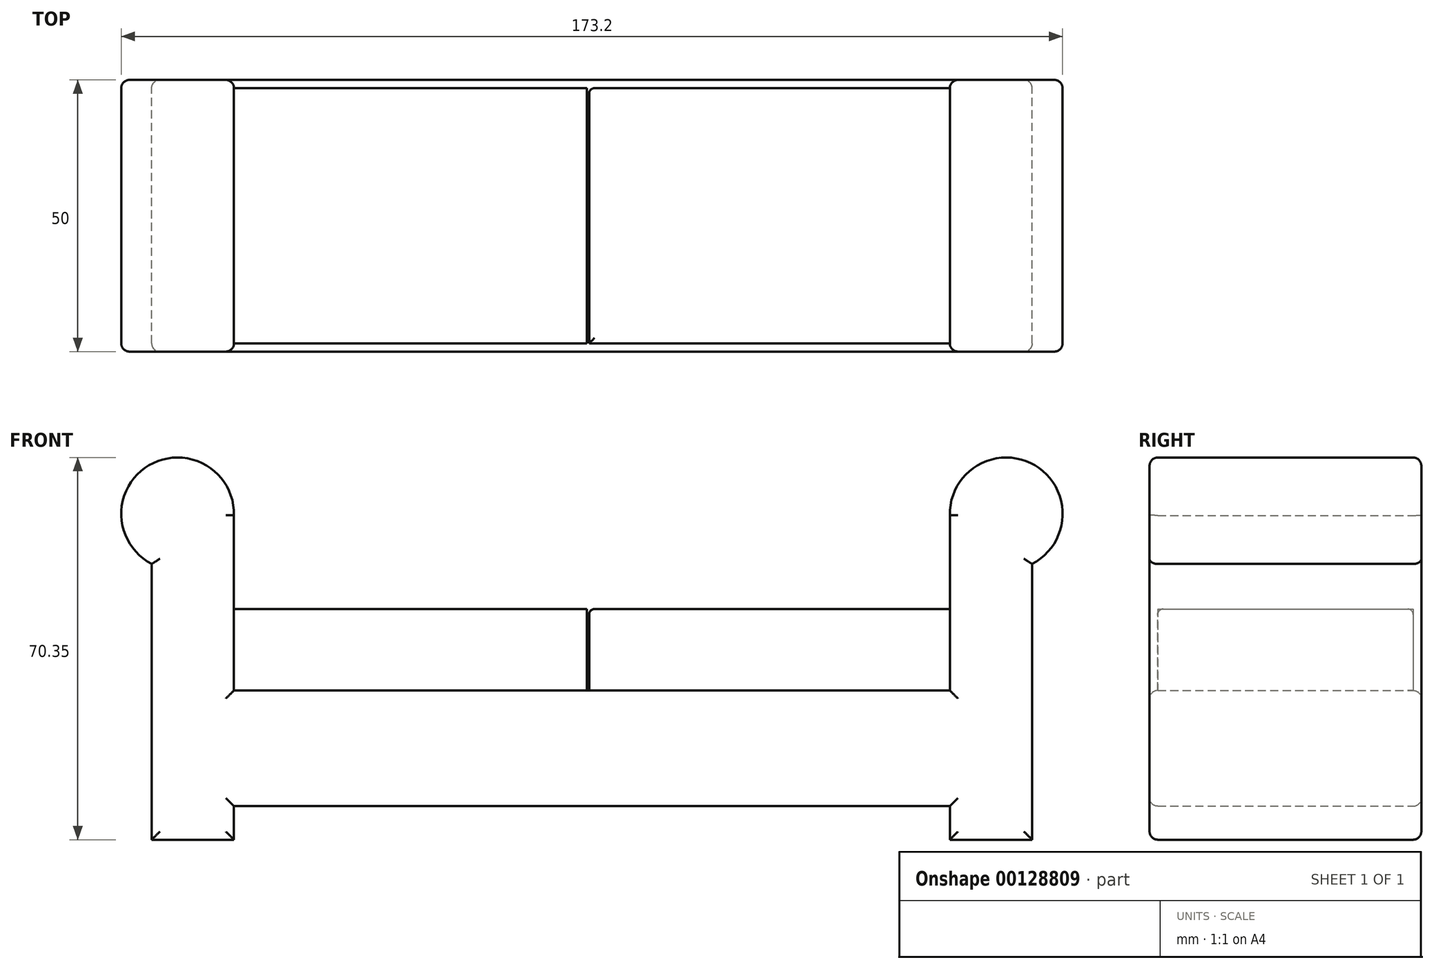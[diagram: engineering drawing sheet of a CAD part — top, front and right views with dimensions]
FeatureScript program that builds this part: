
annotation { "Feature Type Name" : "Feature", "Feature Type Description" : "" }
export const myFeature = defineFeature(function(context is Context, id is Id, definition is map)
    precondition{}
    {
        {
            var Q0;
            Q0=qCreatedBy(makeId("Front.planeOp"),FACE);
            var sketch = newSketch(context, id + "F0", { "sketchPlane" : qUnion([Q0])});
            skLineSegment(sketch, "E0.top", {"start": v(-65.16, -24.52) * mm, "end": v(66.56, -24.52) * mm});
            skLineSegment(sketch, "E0.left", {"start": v(-65.16, 24.24) * mm, "end": v(-65.16, -24.52) * mm});
            skLineSegment(sketch, "E0.right", {"start": v(66.56, -3.22) * mm, "end": v(66.56, -24.52) * mm});
            skPoint(sketch, "E0.middle", {"position": v(0.7, -0.14) * mm});
            skLineSegment(sketch, "E1.bottom", {"start": v(-65.16, -30.69) * mm, "end": v(-80.3, -30.69) * mm});
            skLineSegment(sketch, "E1.left", {"start": v(-65.16, -30.69) * mm, "end": v(-65.16, 29) * mm});
            skLineSegment(sketch, "E1.right", {"start": v(-80.3, -30.69) * mm, "end": v(-80.3, 20.07) * mm});
            skArc(sketch, "E2", {"start": v(-65.16, 29) * mm, "mid": v(-80.8, 38.21) * mm, "end": v(-80.3, 20.07) * mm});
            skPoint(sketch, "E2.second.point", {"position": v(-85.9, 29) * mm});
            skPoint(sketch, "E2.third.point", {"position": v(-75.53, 39.66) * mm});
            skPoint(sketch, "E3.orphan", {"position": v(-80.3, 29) * mm});
            skLineSegment(sketch, "E4", {"start": v(-65.16, -3.22) * mm, "end": v(66.56, -3.22) * mm});
            skPoint(sketch, "E0.bottom.end.orphan", {"position": v(66.56, 24.24) * mm});
            skLineSegment(sketch, "E5", {"start": v(0.7, -3.22) * mm, "end": v(0.7, -24.52) * mm, "construction": true});
            skLineSegment(sketch, "E6.MirrorCS", {"start": v(66.56, 24.24) * mm, "end": v(66.56, -24.52) * mm});
            skPoint(sketch, "E7.MirrorP", {"position": v(76.93, 39.66) * mm});
            skLineSegment(sketch, "E8.MirrorCS", {"start": v(81.7, -30.69) * mm, "end": v(81.7, 20.07) * mm});
            skLineSegment(sketch, "E9.MirrorCS", {"start": v(66.56, -30.69) * mm, "end": v(66.56, 29) * mm});
            skArc(sketch, "E10.MirrorCS", {"start": v(66.56, 29) * mm, "mid": v(82.2, 38.21) * mm, "end": v(81.7, 20.07) * mm});
            skPoint(sketch, "E11.MirrorP", {"position": v(81.7, 29) * mm});
            skPoint(sketch, "E12.MirrorP", {"position": v(87.3, 29) * mm});
            skLineSegment(sketch, "E13.MirrorCS", {"start": v(66.56, -30.69) * mm, "end": v(81.7, -30.69) * mm});
            skSolve(sketch);
        }
        {
            var Q0;
            Q0 = qSketchRegion(id + "F0", true);
            extrude(context, id + "F1", {"entities" : qUnion([Q0]), "endBound" : BoundingType.SYMMETRIC, "depth" : 50 * mm, "offsetDistance" : 25 * mm});
        }
        {
            var Q0;
            Q0=makeQuery(id+"F1.opExtrude","CAP_FACE",FACE,{"disambiguationData":[OSD([sQuery(id+"F0.wireOp",EDGE,"E0.top"),sQuery(id+"F0.wireOp",EDGE,"E0.right"),sQuery(id+"F0.wireOp",EDGE,"E1.bottom"),sQuery(id+"F0.wireOp",EDGE,"E1.left"),sQuery(id+"F0.wireOp",EDGE,"E1.right"),sQuery(id+"F0.wireOp",EDGE,"E2"),sQuery(id+"F0.wireOp",EDGE,"E4")])],"isStart":false});
            var Q1;
            Q1=makeQuery(id+"F1.opExtrude","CAP_FACE",FACE,{"disambiguationData":[OSD([sQuery(id+"F0.wireOp",EDGE,"E0.top"),sQuery(id+"F0.wireOp",EDGE,"E1.bottom"),sQuery(id+"F0.wireOp",EDGE,"E1.left"),sQuery(id+"F0.wireOp",EDGE,"E1.right"),sQuery(id+"F0.wireOp",EDGE,"E2"),sQuery(id+"F0.wireOp",EDGE,"E4"),sQuery(id+"F0.wireOp",EDGE,"E8.MirrorCS"),sQuery(id+"F0.wireOp",EDGE,"E9.MirrorCS"),sQuery(id+"F0.wireOp",EDGE,"E10.MirrorCS"),sQuery(id+"F0.wireOp",EDGE,"E13.MirrorCS")])],"isStart":true});
            fillet(context, id + "F2", {"entities" : qUnion([Q0, Q1]), "radius" : 1.5 * mm, "tangentPropagation" : true, "allowEdgeOverflow" : false});
        }
        {
            var Q0;
            Q0=makeQuery(id+"F1.opExtrude","SWEPT_FACE",FACE,{"disambiguationData":[OSD([sQuery(id+"F0.wireOp",EDGE,"E4")])]});
            var sketch = newSketch(context, id + "F3", { "sketchPlane" : qUnion([Q0])});
            skLineSegment(sketch, "E14.bottom", {"start": v(-65.16, -23.5) * mm, "end": v(-0.2, -23.5) * mm});
            skLineSegment(sketch, "E14.top", {"start": v(-65.16, 25.3) * mm, "end": v(-0.2, 25.3) * mm});
            skLineSegment(sketch, "E14.left", {"start": v(-65.16, -23.5) * mm, "end": v(-65.16, 25.3) * mm});
            skLineSegment(sketch, "E14.right", {"start": v(66.56, -23.5) * mm, "end": v(66.56, 25.3) * mm});
            skLineSegment(sketch, "E15", {"start": v(0, 25.3) * mm, "end": v(0, -23.5) * mm, "construction": true});
            skLineSegment(sketch, "E16", {"start": v(-0.2, -23.5) * mm, "end": v(-0.2, 25.3) * mm});
            skLineSegment(sketch, "E17", {"start": v(0.2, -23.5) * mm, "end": v(0.2, 25.3) * mm});
            skLineSegment(sketch, "E18.trimOffspring", {"start": v(0.2, 25.3) * mm, "end": v(66.56, 25.3) * mm});
            skLineSegment(sketch, "E19.trimOffspring", {"start": v(0.2, -23.5) * mm, "end": v(66.56, -23.5) * mm});
            skSolve(sketch);
        }
        {
            var Q0;
            {var subQ0=sQuery(id+"F3.wireOp",EDGE,"E14.left");var subQ1=sQuery(id+"F3.wireOp",EDGE,"E14.bottom");var subQ2=makeQuery(id+"F3.imprint","INTERSECT",VERTEX,{"derivedFrom":[subQ1,subQ0]});Q0=makeQuery(id+"F3.imprint","IMPRINT",FACE,{"disambiguationData":[TD([[makeQuery(id+"F3.imprint","IMPRINT",EDGE,{"disambiguationData":[TD([[subQ2,-1.0]])],"derivedFrom":subQ1}),1.0]])]});}
            extrude(context, id + "F4", {"entities" : qUnion([Q0]), "operationType" : NewBodyOperationType.ADD, "depth" : 15 * mm, "offsetDistance" : 25 * mm});
        }
        {
            var Q0;
            {var subQ5=sQuery(id+"F3.wireOp",EDGE,"E19.trimOffspring");Q0=makeQuery(id+"F3.imprint","IMPRINT",FACE,{"disambiguationData":[TD([[makeQuery(id+"F3.imprint","IMPRINT",EDGE,{"derivedFrom":subQ5}),1.0]])]});}
            extrude(context, id + "F5", {"entities" : qUnion([Q0]), "operationType" : NewBodyOperationType.ADD, "depth" : 15 * mm, "offsetDistance" : 25 * mm});
        }
        {
            var Q0;
            Q0=makeQuery(id+"F5.opExtrude","CAP_EDGE",EDGE,{"disambiguationData":[OSD([sQuery(id+"F3.wireOp",EDGE,"E17")])],"isStart":false});
            var Q1;
            Q1=makeQuery(id+"F5.opExtrude","CAP_EDGE",EDGE,{"disambiguationData":[OSD([sQuery(id+"F3.wireOp",EDGE,"E19.trimOffspring")])],"isStart":false});
            var Q2;
            Q2=makeQuery(id+"F5.opExtrude","CAP_EDGE",EDGE,{"disambiguationData":[OSD([sQuery(id+"F0.wireOp",EDGE,"E4")])],"isStart":false});
            var Q3;
            Q3=makeQuery(id+"F5.opExtrude","SWEPT_EDGE",EDGE,{"disambiguationData":[OSD([sQuery(id+"F0.wireOp",EDGE,"E4"),sQuery(id+"F3.wireOp",EDGE,"E17")])]});
            fillet(context, id + "F6", {"entities" : qUnion([Q0, Q1, Q2, Q3]), "radius" : 1 * mm, "tangentPropagation" : true, "allowEdgeOverflow" : false});
        }
    });
